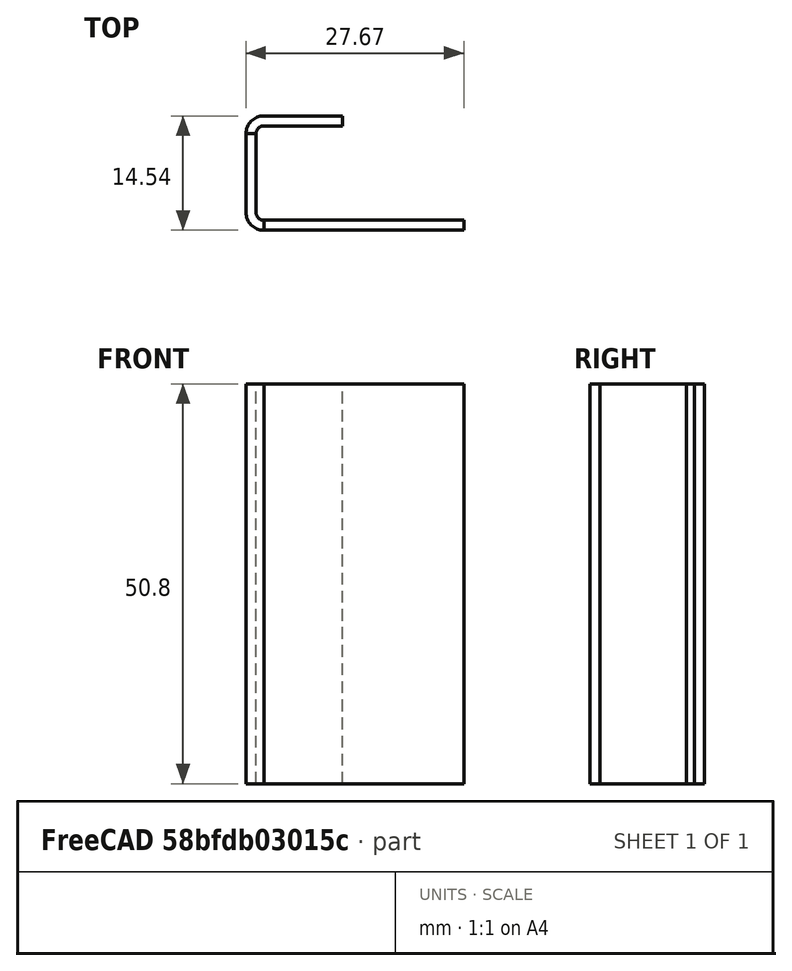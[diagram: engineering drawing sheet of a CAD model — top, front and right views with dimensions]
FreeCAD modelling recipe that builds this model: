
FCSTD DOCUMENT  (FreeCAD 0.16R6706 (Git))
Label: test
License: All rights reserved
LicenseURL: http://en.wikipedia.org/wiki/All_rights_reserved
objects: Part::FeaturePython×2, Part::Box×1
note: 3 computed .brp shape members not serialized (recipe doc carries the construction recipe); baked Part::Feature solids carry a one-line shape summary decoded from their .brp

FEATURE [Part::Box] Box  label="Cube"
  Height = 50.8
  Length = 25.4
  Width = 1.27
FEATURE [Part::FeaturePython] Bend  # WARN: FeaturePython — macro-defined, semantics opaque (R4)
  angle = 90
  baseObject = -> Box [Face1]
  gap1 = 0
  gap2 = 0
  invert = false
  length = 10
  miterangle1 = 0
  miterangle2 = 0
  radius = 1
  reliefd = 1
  reliefw = 0.5
FEATURE [Part::FeaturePython] Bend001  # WARN: FeaturePython — macro-defined, semantics opaque (R4)
  angle = 90
  baseObject = -> Bend [Face1]
  gap1 = 0
  gap2 = 0
  invert = false
  length = 10
  miterangle1 = 0
  miterangle2 = 0
  radius = 1
  reliefd = 1
  reliefw = 0.5
